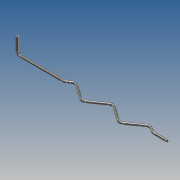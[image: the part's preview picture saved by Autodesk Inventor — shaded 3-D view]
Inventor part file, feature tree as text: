
AUTODESK INVENTOR PART (.ipt)
format: ipt  version: 2016 (Build 200138000, 138)  size: 115,712 bytes
history: native  units: mm
features: sketch x3, plane x1, sweep x1
ambient origin geometry x8: Origin, YZ Plane, XZ Plane, XY Plane, X Axis, Y Axis, Z Axis, Center Point
bodies: Body1 (feature_tree)
feature tree (5):
  sketch  "Sketch1"  dims[d0=160.0mm d1=50.0mm]
  sketch  "3D Sketch1"
  plane  "Work Plane1"
  sweep  "Sweep2"
  sketch  "Sketch2"  dims[d2=20.0mm d3=20.0mm d4=20.0mm d5=20.0mm d6=20.0mm d7=14.0mm d8=5.0mm d9=15.714286mm d11=2.5mm d14=5.0mm d15=17.0mm d16=90.0deg d17=3.0mm d18=0.0mm d19=0.0mm]
